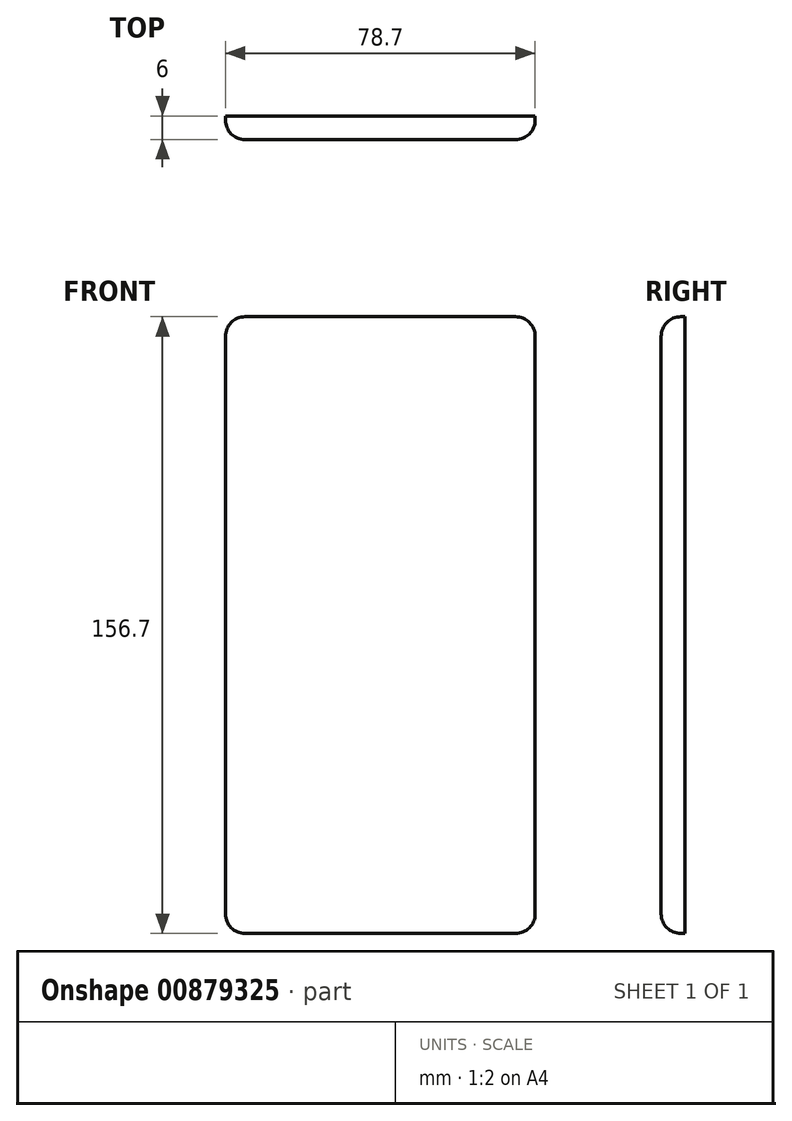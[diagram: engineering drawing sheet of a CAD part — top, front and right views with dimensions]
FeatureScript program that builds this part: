
annotation { "Feature Type Name" : "Feature", "Feature Type Description" : "" }
export const myFeature = defineFeature(function(context is Context, id is Id, definition is map)
    precondition{}
    {
        {
            var Q0;
            Q0=qCreatedBy(makeId("Front.planeOp"),FACE);
            var sketch = newSketch(context, id + "F0", { "sketchPlane" : qUnion([Q0])});
            skLineSegment(sketch, "E0.bottom", {"start": v(0, 0) * mm, "end": v(74.7, 0) * mm});
            skLineSegment(sketch, "E0.top", {"start": v(0, 152.7) * mm, "end": v(74.7, 152.7) * mm});
            skLineSegment(sketch, "E0.left", {"start": v(0, 0) * mm, "end": v(0, 152.7) * mm});
            skLineSegment(sketch, "E0.right", {"start": v(74.7, 0) * mm, "end": v(74.7, 152.7) * mm});
            skLineSegment(sketch, "E1", {"start": v(-2, 154.7) * mm, "end": v(-2, -2) * mm});
            skLineSegment(sketch, "E2", {"start": v(-2, -2) * mm, "end": v(76.7, -2) * mm});
            skLineSegment(sketch, "E3", {"start": v(76.7, -2) * mm, "end": v(76.7, 154.7) * mm});
            skLineSegment(sketch, "E4", {"start": v(76.7, 154.7) * mm, "end": v(-2, 154.7) * mm});
            skSolve(sketch);
        }
        {
            var Q0;
            Q0=makeQuery(id+"F0.imprint","IMPRINT",FACE,{"disambiguationData":[TD([[makeQuery(id+"F0.imprint","IMPRINT",EDGE,{"derivedFrom":sQuery(id+"F0.wireOp",EDGE,"E0.bottom")}),-1.0]])]});
            var Q1;
            Q1=makeQuery(id+"F0.imprint","IMPRINT",FACE,{"disambiguationData":[TD([[makeQuery(id+"F0.imprint","IMPRINT",EDGE,{"derivedFrom":sQuery(id+"F0.wireOp",EDGE,"E0.bottom")}),1.0]])]});
            extrude(context, id + "F1", {"entities" : qUnion([Q0, Q1]), "depth" : 6 * mm, "offsetDistance" : 25 * mm});
        }
        {
            var Q0;
            Q0=makeQuery(id+"F1.opExtrude","SWEPT_EDGE",EDGE,{"disambiguationData":[OSD([sQuery(id+"F0.wireOp",EDGE,"E1"),sQuery(id+"F0.wireOp",EDGE,"E2")])]});
            var Q1;
            Q1=makeQuery(id+"F1.opExtrude","SWEPT_EDGE",EDGE,{"disambiguationData":[OSD([sQuery(id+"F0.wireOp",EDGE,"E2"),sQuery(id+"F0.wireOp",EDGE,"E3")])]});
            var Q2;
            Q2=makeQuery(id+"F1.opExtrude","SWEPT_EDGE",EDGE,{"disambiguationData":[OSD([sQuery(id+"F0.wireOp",EDGE,"E1"),sQuery(id+"F0.wireOp",EDGE,"E4")])]});
            var Q3;
            Q3=makeQuery(id+"F1.opExtrude","SWEPT_EDGE",EDGE,{"disambiguationData":[OSD([sQuery(id+"F0.wireOp",EDGE,"E3"),sQuery(id+"F0.wireOp",EDGE,"E4")])]});
            fillet(context, id + "F2", {"entities" : qUnion([Q0, Q1, Q2, Q3]), "radius" : 5 * mm, "tangentPropagation" : true, "allowEdgeOverflow" : false});
        }
        {
            var Q0;
            Q0=makeQuery(id+"F1.opExtrude","CAP_FACE",FACE,{"disambiguationData":[OSD([sQuery(id+"F0.wireOp",EDGE,"E1"),sQuery(id+"F0.wireOp",EDGE,"E2"),sQuery(id+"F0.wireOp",EDGE,"E3"),sQuery(id+"F0.wireOp",EDGE,"E4")])],"isStart":false});
            fillet(context, id + "F3", {"entities" : qUnion([Q0]), "radius" : 5 * mm, "tangentPropagation" : true, "allowEdgeOverflow" : false});
        }
    });
